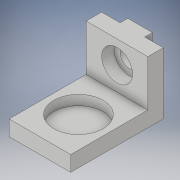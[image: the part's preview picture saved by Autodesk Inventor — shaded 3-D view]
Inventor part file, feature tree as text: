
AUTODESK INVENTOR PART (.ipt)
format: ipt  version: 2019 (Build 230136000, 136)  size: 138,752 bytes
history: native  units: in
note: dims shown in document units (in); Inventor stores cm internally (conversion verified against a paired STEP export)
features: sketch x4, projected_geometry x3, extrude x2, hole x2
ambient origin geometry x8: Origin, YZ Plane, XZ Plane, XY Plane, X Axis, Y Axis, Z Axis, Center Point
bodies: Solid1 (feature_tree)
feature tree (11):
  extrude  "Extrusion1"  Depth=0.5in
  hole  "Hole2"  [1 undecoded]
  extrude  "Extrusion2"  Depth=0.2in
  hole  "Hole3"  [1 undecoded]
  sketch  "Sketch1"  dims[d0=0.125in d1=0.5in]
  sketch  "Sketch3"  dims[d4=0.125in d5=0.75in]
  projected_geometry  "Projected Loop2"
  sketch  "Sketch4"  dims[d6=0.5in d7=0.0in]
  projected_geometry  "Projected Loop3"
  sketch  "Sketch5"  dims[d15=0.4in d16=0.75in d17=0.375in d18=0.25in d19=0.5635in d20=0.08in d21=0.0in d22=0.2in d23=0.5in d24=0.15in d25=0.0625in d26=0.0in d27=0.15in d28=0.75in d29=0.25in d30=0.1in d31=0.5635in d32=1.0in d33=0.8108in]
  projected_geometry  "Projected Loop4"
note: 2 required parameter values undecoded (feature->parameter linkage not recoverable at this tier; creation-order binding heuristic only, values carry confidence <= 0.55)
